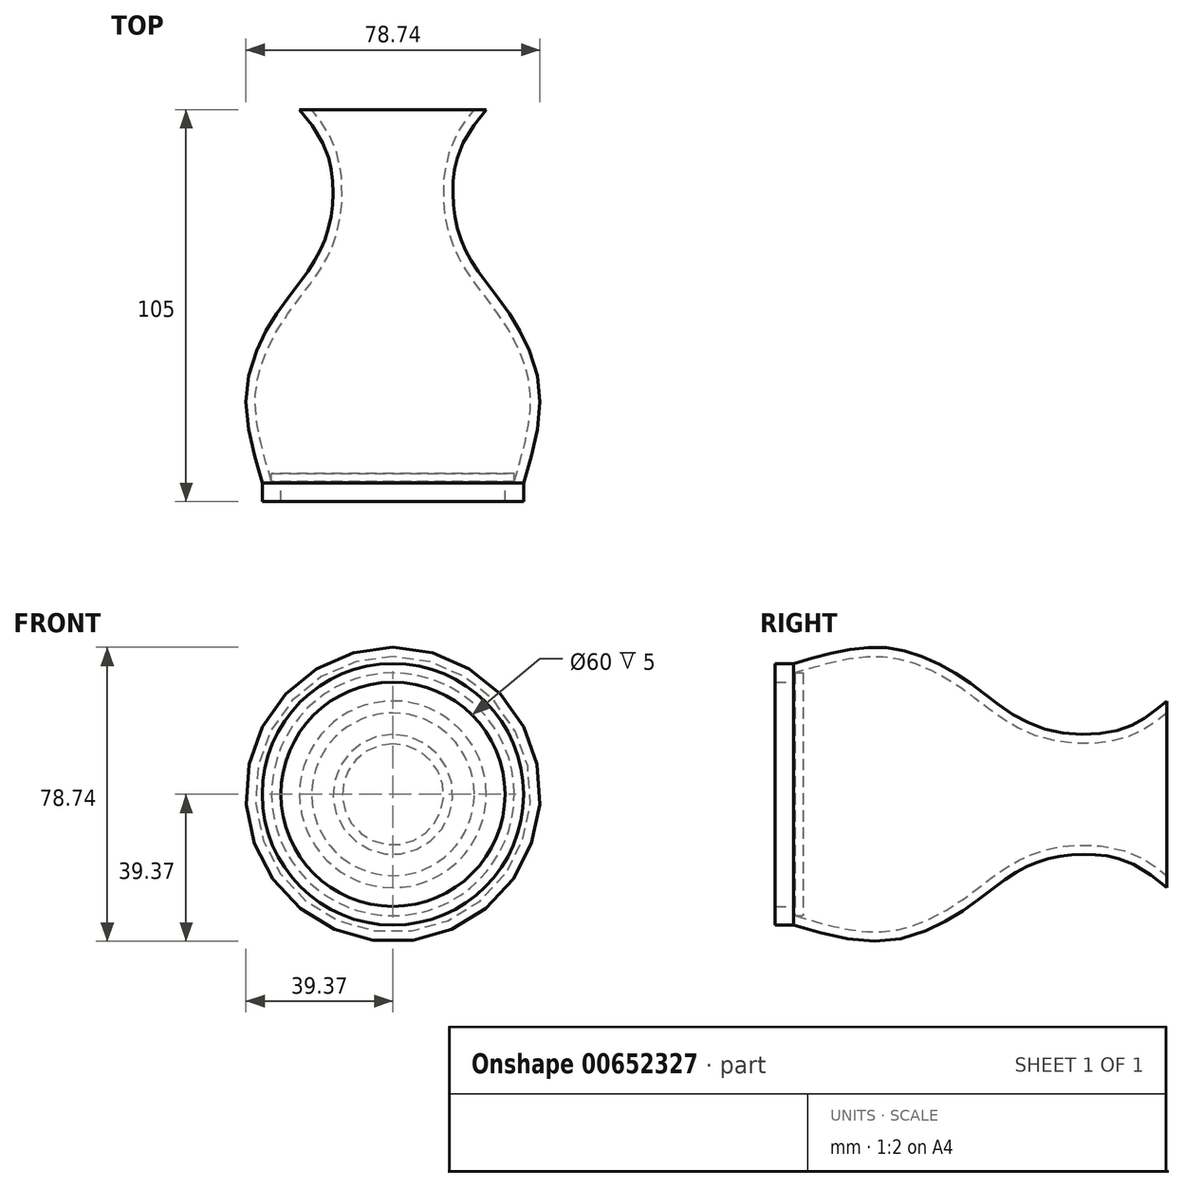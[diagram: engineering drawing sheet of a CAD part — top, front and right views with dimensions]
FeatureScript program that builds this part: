
annotation { "Feature Type Name" : "Feature", "Feature Type Description" : "" }
export const myFeature = defineFeature(function(context is Context, id is Id, definition is map)
    precondition{}
    {
        {
            var Q0;
            Q0=qCreatedBy(makeId("Top.planeOp"),FACE);
            var sketch = newSketch(context, id + "F0", { "sketchPlane" : qUnion([Q0])});
            skLineSegment(sketch, "E0", {"start": v(25, 63.46) * mm, "end": v(0, 63.46) * mm});
            skLineSegment(sketch, "E1", {"start": v(0, 63.46) * mm, "end": v(0, -36.54) * mm});
            skLineSegment(sketch, "E2", {"start": v(0, -36.54) * mm, "end": v(30, -36.54) * mm});
            skLineSegment(sketch, "E3", {"start": v(30, -36.54) * mm, "end": v(30, -41.54) * mm});
            skLineSegment(sketch, "E4", {"start": v(30, -41.54) * mm, "end": v(35, -41.54) * mm});
            skLineSegment(sketch, "E5", {"start": v(35, -41.54) * mm, "end": v(35, -36.54) * mm});
            skFitSpline(sketch, "E6", {"points": [v(25, 63.46) * mm, v(17.28, 50.7) * mm, v(18.37, 28.2) * mm, v(30.3, 10.05) * mm, v(39.24, -11.63) * mm, v(35, -36.54) * mm], "startDerivative": vector(-55.18, -66.93) * mm, "endDerivative": vector(-34.47, -116.11) * mm});
            skSolve(sketch);
        }
        {
            var Q0;
            Q0=makeQuery(id+"F0.imprint","IMPRINT",FACE,{"disambiguationData":[TD([[makeQuery(id+"F0.imprint","IMPRINT",EDGE,{"derivedFrom":sQuery(id+"F0.wireOp",EDGE,"E0")}),1.0]])]});
            var Q1;
            Q1=sQuery(id+"F0.wireOp",EDGE,"E1");
            revolve(context, id + "F1", {"surfaceOperationType" : NewSurfaceOperationType.NEW, "entities" : qUnion([Q0]), "axis" : qUnion([Q1]), "revolveType" : RevolveType.FULL});
        }
        {
            var Q0;
            Q0=makeQuery(id+"F1.opRevolve","SWEPT_FACE",FACE,{"disambiguationData":[OSD([sQuery(id+"F0.wireOp",EDGE,"E0")])]});
            shell(context, id + "F2", {"entities" : qUnion([Q0]), "thickness" : 2.5 * mm});
        }
    });
